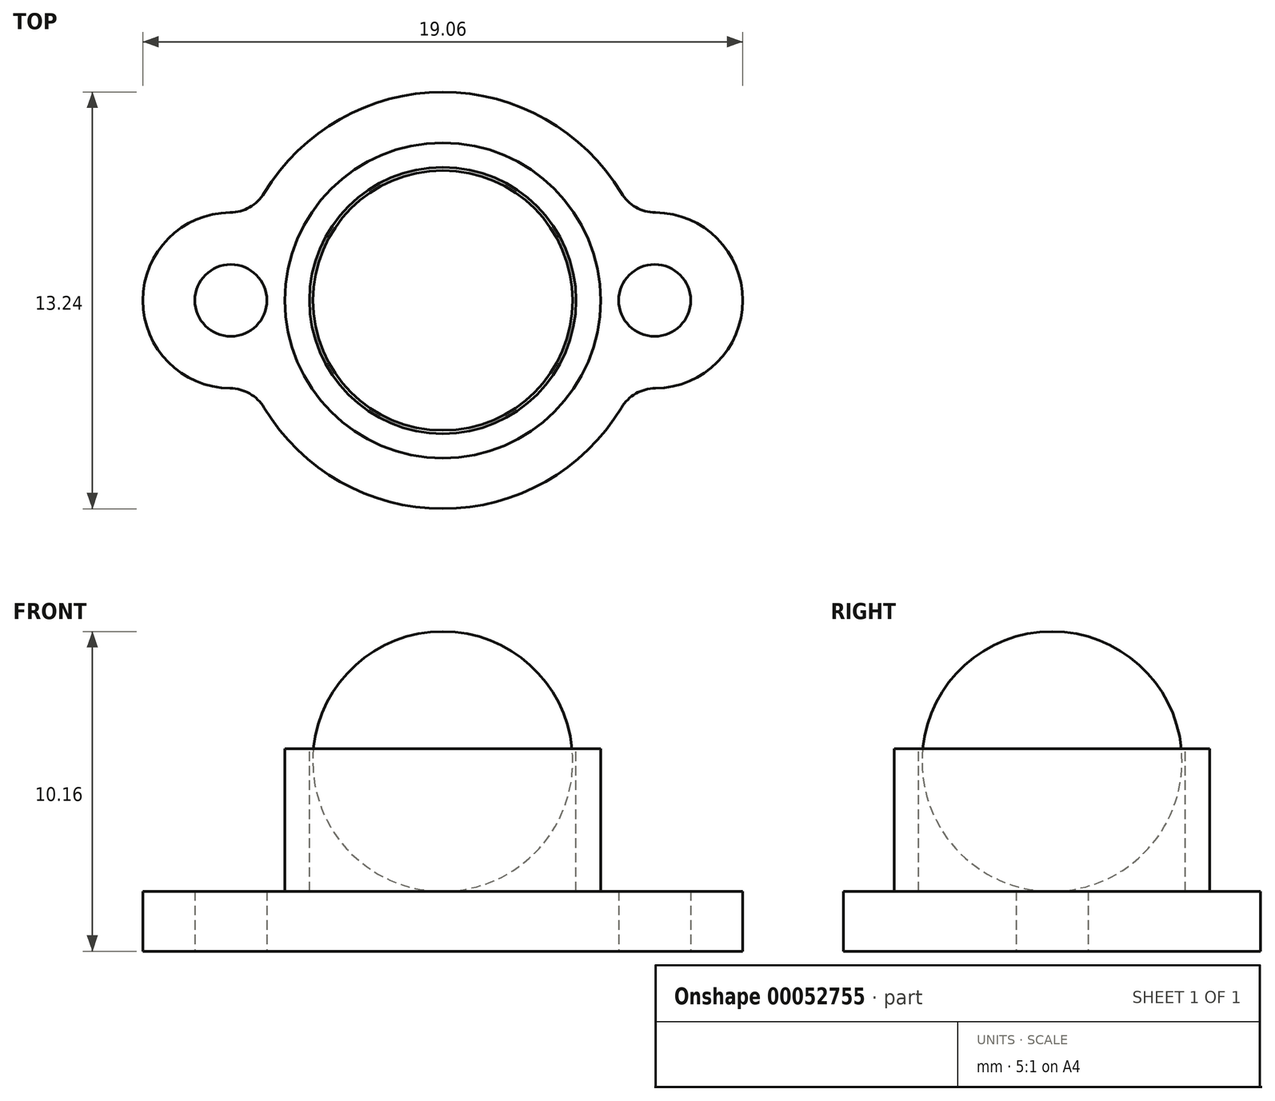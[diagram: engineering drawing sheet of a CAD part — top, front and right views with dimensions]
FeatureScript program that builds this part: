
annotation { "Feature Type Name" : "Feature", "Feature Type Description" : "" }
export const myFeature = defineFeature(function(context is Context, id is Id, definition is map)
    precondition{}
    {
        {
            var Q0;
            Q0=qCreatedBy(makeId("Top.planeOp"),FACE);
            var sketch = newSketch(context, id + "F0", { "sketchPlane" : qUnion([Q0])});
            skArc(sketch, "E0", {"start": v(-5.67, -3.4) * mm, "mid": v(0, -6.62) * mm, "end": v(5.67, -3.4) * mm});
            skCircle(sketch, "E1", {"center": v(-6.73, 0) * mm, "radius": 1.14 * mm});
            skArc(sketch, "E2", {"start": v(-6.75, 2.8) * mm, "mid": v(-9.53, 0) * mm, "end": v(-6.75, -2.8) * mm});
            skPoint(sketch, "E3.visualSharp", {"position": v(-6.04, 2.7) * mm});
            skArc(sketch, "E3.filletArc", {"start": v(-6.75, 2.8) * mm, "mid": v(-6.13, 2.96) * mm, "end": v(-5.67, 3.4) * mm});
            skPoint(sketch, "E4.visualSharp", {"position": v(-6.04, -2.7) * mm});
            skArc(sketch, "E4.filletArc", {"start": v(-5.67, -3.4) * mm, "mid": v(-6.13, -2.96) * mm, "end": v(-6.75, -2.8) * mm});
            skArc(sketch, "E5.MirrorCS", {"start": v(5.67, -3.4) * mm, "mid": v(6.13, -2.96) * mm, "end": v(6.75, -2.8) * mm});
            skArc(sketch, "E6.MirrorCS", {"start": v(6.75, 2.8) * mm, "mid": v(6.13, 2.96) * mm, "end": v(5.67, 3.4) * mm});
            skPoint(sketch, "E7.MirrorP", {"position": v(6.04, -2.7) * mm});
            skCircle(sketch, "E8.MirrorC", {"center": v(6.73, 0) * mm, "radius": 1.14 * mm});
            skArc(sketch, "E9.MirrorCS", {"start": v(6.75, 2.8) * mm, "mid": v(9.53, 0) * mm, "end": v(6.75, -2.8) * mm});
            skPoint(sketch, "E10.MirrorP", {"position": v(6.04, 2.7) * mm});
            skArc(sketch, "E11.trimOffspring", {"start": v(5.67, 3.4) * mm, "mid": v(0, 6.62) * mm, "end": v(-5.67, 3.4) * mm});
            skSolve(sketch);
        }
        {
            var Q0;
            Q0 = qSketchRegion(id + "F0", true);
            extrude(context, id + "F1", {"entities" : qUnion([Q0]), "depth" : 1.9 * mm});
        }
        {
            var Q0;
            Q0=qCreatedBy(makeId("Front.planeOp"),FACE);
            var sketch = newSketch(context, id + "F2", { "sketchPlane" : qUnion([Q0])});
            skLineSegment(sketch, "E12", {"start": v(0, 10.16) * mm, "end": v(0, 1.9) * mm});
            skArc(sketch, "E13", {"start": v(0, 1.9) * mm, "mid": v(4.13, 6.03) * mm, "end": v(0, 10.16) * mm});
            skSolve(sketch);
        }
        {
            var Q0;
            Q0 = qSketchRegion(id + "F2", true);
            var Q1;
            Q1=sQuery(id+"F2.wireOp",EDGE,"E12");
            revolve(context, id + "F3", {"entities" : qUnion([Q0]), "axis" : qUnion([Q1]), "revolveType" : RevolveType.FULL});
        }
        {
            var Q0;
            Q0=qCreatedBy(makeId("Front.planeOp"),FACE);
            var sketch = newSketch(context, id + "F4", { "sketchPlane" : qUnion([Q0])});
            skLineSegment(sketch, "E14", {"start": v(4.23, 1.9) * mm, "end": v(4.23, 6.43) * mm});
            skLineSegment(sketch, "E15", {"start": v(4.23, 6.43) * mm, "end": v(5.01, 6.43) * mm});
            skLineSegment(sketch, "E16", {"start": v(5.01, 6.43) * mm, "end": v(5.01, 1.9) * mm});
            skLineSegment(sketch, "E17", {"start": v(5.01, 1.9) * mm, "end": v(4.23, 1.9) * mm});
            skLineSegment(sketch, "E18", {"start": v(0, 11.69) * mm, "end": v(0, -1.92) * mm, "construction": true});
            skSolve(sketch);
        }
        {
            var Q0;
            Q0=makeQuery(id+"F4.imprint","IMPRINT",FACE,{"disambiguationData":[TD([[makeQuery(id+"F4.imprint","IMPRINT",EDGE,{"derivedFrom":sQuery(id+"F4.wireOp",EDGE,"E14")}),-1.0]])]});
            var Q1;
            Q1=sQuery(id+"F4.wireOp",EDGE,"E18");
            revolve(context, id + "F5", {"operationType" : NewBodyOperationType.ADD, "entities" : qUnion([Q0]), "axis" : qUnion([Q1]), "revolveType" : RevolveType.FULL});
        }
    });
